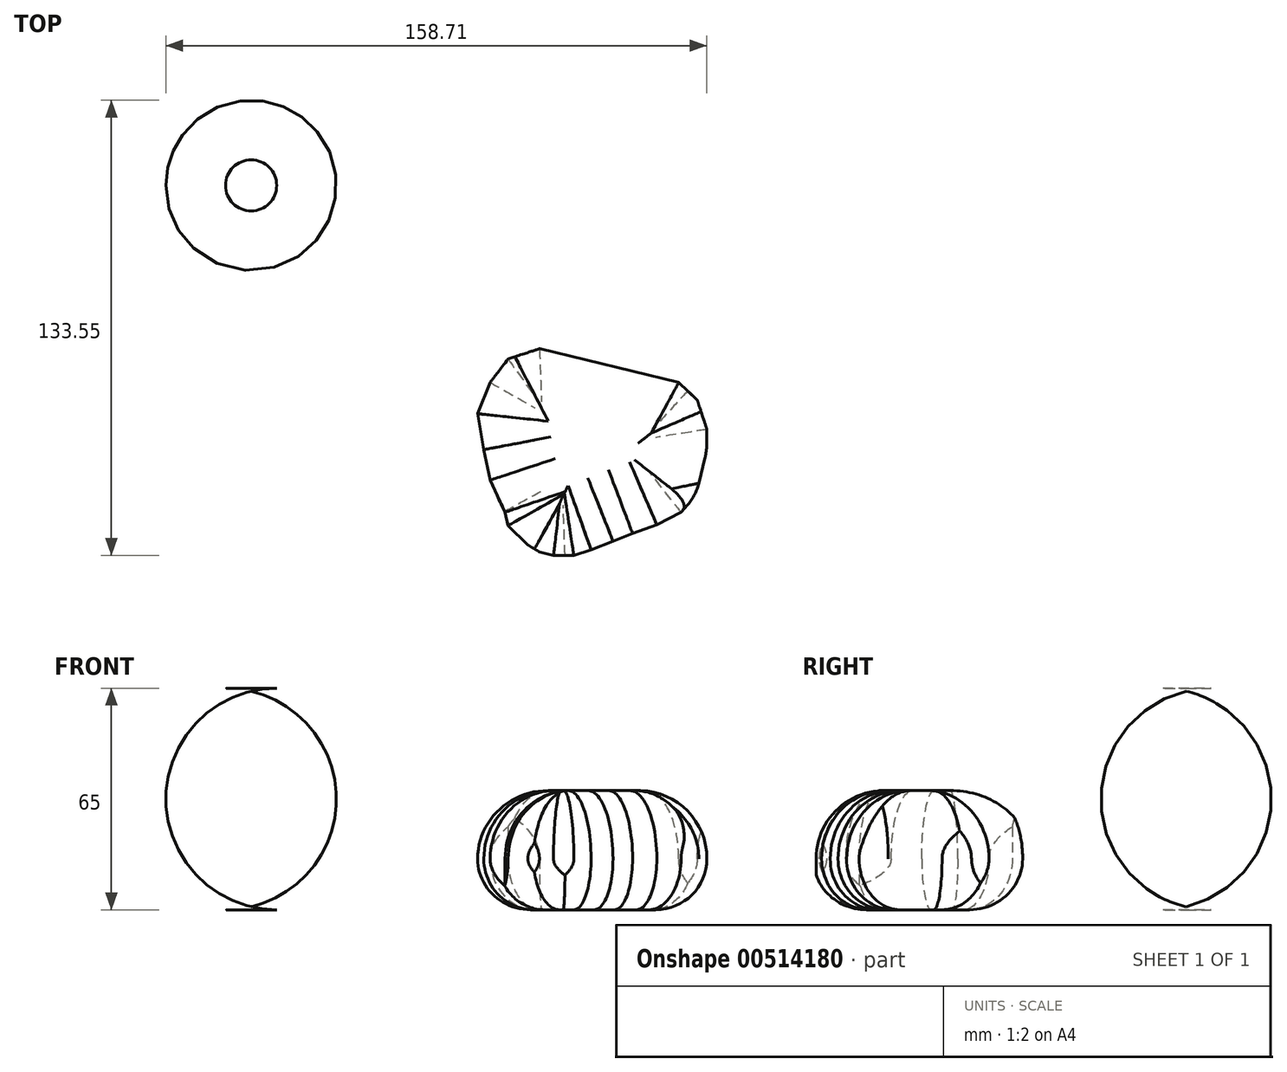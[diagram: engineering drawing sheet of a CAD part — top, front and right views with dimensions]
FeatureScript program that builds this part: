
annotation { "Feature Type Name" : "Feature", "Feature Type Description" : "" }
export const myFeature = defineFeature(function(context is Context, id is Id, definition is map)
    precondition{}
    {
        {
            var Q0;
            Q0=qCreatedBy(makeId("Top.planeOp"),FACE);
            var sketch = newSketch(context, id + "F0", { "sketchPlane" : qUnion([Q0])});
            skCircle(sketch, "E0", {"center": v(-39.49, 24.57) * mm, "radius": 45 * mm});
            skLineSegment(sketch, "E1", {"start": v(19.29, -34.44) * mm, "end": v(22.96, -25.26) * mm});
            skLineSegment(sketch, "E2", {"start": v(22.96, -25.26) * mm, "end": v(28.24, -18.37) * mm});
            skLineSegment(sketch, "E3", {"start": v(28.24, -18.37) * mm, "end": v(37.42, -15.38) * mm});
            skLineSegment(sketch, "E4", {"start": v(37.42, -15.38) * mm, "end": v(78.3, -25.26) * mm});
            skLineSegment(sketch, "E5", {"start": v(78.3, -25.26) * mm, "end": v(83.7, -30.4) * mm});
            skLineSegment(sketch, "E6", {"start": v(83.7, -30.4) * mm, "end": v(86.56, -39.03) * mm});
            skLineSegment(sketch, "E7", {"start": v(86.56, -39.03) * mm, "end": v(86.56, -45) * mm});
            skLineSegment(sketch, "E8", {"start": v(86.56, -45) * mm, "end": v(84.97, -51.55) * mm});
            skLineSegment(sketch, "E9", {"start": v(84.97, -51.55) * mm, "end": v(83.33, -58.36) * mm});
            skLineSegment(sketch, "E10", {"start": v(83.33, -58.36) * mm, "end": v(78.98, -63.37) * mm});
            skLineSegment(sketch, "E11", {"start": v(78.98, -63.37) * mm, "end": v(71.86, -67.04) * mm});
            skLineSegment(sketch, "E12", {"start": v(71.86, -67.04) * mm, "end": v(64.74, -69.57) * mm});
            skLineSegment(sketch, "E13", {"start": v(64.74, -69.57) * mm, "end": v(59, -71.86) * mm});
            skLineSegment(sketch, "E14", {"start": v(59, -71.86) * mm, "end": v(52.58, -74.39) * mm});
            skLineSegment(sketch, "E15", {"start": v(41.56, -76) * mm, "end": v(37.42, -75) * mm});
            skLineSegment(sketch, "E16", {"start": v(37.42, -75) * mm, "end": v(34.02, -72.92) * mm});
            skLineSegment(sketch, "E17", {"start": v(34.02, -72.92) * mm, "end": v(28.24, -67.27) * mm});
            skLineSegment(sketch, "E18", {"start": v(28.24, -67.27) * mm, "end": v(27.33, -63.37) * mm});
            skLineSegment(sketch, "E19", {"start": v(27.33, -63.37) * mm, "end": v(22.96, -53.96) * mm});
            skLineSegment(sketch, "E20", {"start": v(22.96, -53.96) * mm, "end": v(21.08, -45) * mm});
            skLineSegment(sketch, "E21", {"start": v(21.08, -45) * mm, "end": v(19.29, -34.44) * mm});
            skLineSegment(sketch, "E22", {"start": v(52.58, -74.39) * mm, "end": v(47.53, -76) * mm});
            skLineSegment(sketch, "E23", {"start": v(47.53, -76) * mm, "end": v(41.56, -76) * mm});
            skSolve(sketch);
        }
        {
            var Q0;
            Q0=makeQuery(id+"F0.imprint","IMPRINT",FACE,{"disambiguationData":[TD([[makeQuery(id+"F0.imprint","IMPRINT",EDGE,{"derivedFrom":sQuery(id+"F0.wireOp",EDGE,"E1")}),-1.0]])]});
            extrude(context, id + "F1", {"entities" : qUnion([Q0]), "depth" : 35 * mm});
        }
        {
            var Q0;
            Q0=makeQuery(id+"F1.opExtrude","CAP_EDGE",EDGE,{"disambiguationData":[OSD([sQuery(id+"F0.wireOp",EDGE,"E20")])],"isStart":false});
            var Q1;
            Q1=makeQuery(id+"F1.opExtrude","CAP_EDGE",EDGE,{"disambiguationData":[OSD([sQuery(id+"F0.wireOp",EDGE,"E1")])],"isStart":false});
            var Q2;
            Q2=makeQuery(id+"F1.opExtrude","CAP_EDGE",EDGE,{"disambiguationData":[OSD([sQuery(id+"F0.wireOp",EDGE,"E3")])],"isStart":false});
            var Q3;
            Q3=makeQuery(id+"F1.opExtrude","CAP_EDGE",EDGE,{"disambiguationData":[OSD([sQuery(id+"F0.wireOp",EDGE,"E4")])],"isStart":false});
            var Q4;
            Q4=makeQuery(id+"F1.opExtrude","CAP_EDGE",EDGE,{"disambiguationData":[OSD([sQuery(id+"F0.wireOp",EDGE,"E2")])],"isStart":false});
            var Q5;
            Q5=makeQuery(id+"F1.opExtrude","CAP_EDGE",EDGE,{"disambiguationData":[OSD([sQuery(id+"F0.wireOp",EDGE,"E5")])],"isStart":false});
            var Q6;
            Q6=makeQuery(id+"F1.opExtrude","SWEPT_EDGE",EDGE,{"disambiguationData":[OSD([sQuery(id+"F0.wireOp",EDGE,"E7"),sQuery(id+"F0.wireOp",EDGE,"E8")])]});
            var Q7;
            Q7=makeQuery(id+"F1.opExtrude","CAP_EDGE",EDGE,{"disambiguationData":[OSD([sQuery(id+"F0.wireOp",EDGE,"E7")])],"isStart":false});
            var Q8;
            Q8=makeQuery(id+"F1.opExtrude","CAP_EDGE",EDGE,{"disambiguationData":[OSD([sQuery(id+"F0.wireOp",EDGE,"E10")])],"isStart":false});
            var Q9;
            Q9=makeQuery(id+"F1.opExtrude","CAP_EDGE",EDGE,{"disambiguationData":[OSD([sQuery(id+"F0.wireOp",EDGE,"E8"),sQuery(id+"F0.wireOp",EDGE,"E9")])],"isStart":false});
            var Q10;
            Q10=makeQuery(id+"F1.opExtrude","CAP_EDGE",EDGE,{"disambiguationData":[OSD([sQuery(id+"F0.wireOp",EDGE,"E12")])],"isStart":false});
            var Q11;
            Q11=makeQuery(id+"F1.opExtrude","CAP_EDGE",EDGE,{"disambiguationData":[OSD([sQuery(id+"F0.wireOp",EDGE,"E11")])],"isStart":false});
            var Q12;
            Q12=makeQuery(id+"F1.opExtrude","CAP_EDGE",EDGE,{"disambiguationData":[OSD([sQuery(id+"F0.wireOp",EDGE,"E13")])],"isStart":false});
            var Q13;
            Q13=makeQuery(id+"F1.opExtrude","CAP_EDGE",EDGE,{"disambiguationData":[OSD([sQuery(id+"F0.wireOp",EDGE,"E23")])],"isStart":false});
            var Q14;
            Q14=makeQuery(id+"F1.opExtrude","CAP_EDGE",EDGE,{"disambiguationData":[OSD([sQuery(id+"F0.wireOp",EDGE,"E22")])],"isStart":false});
            var Q15;
            Q15=makeQuery(id+"F1.opExtrude","CAP_EDGE",EDGE,{"disambiguationData":[OSD([sQuery(id+"F0.wireOp",EDGE,"E14")])],"isStart":false});
            var Q16;
            Q16=makeQuery(id+"F1.opExtrude","CAP_EDGE",EDGE,{"disambiguationData":[OSD([sQuery(id+"F0.wireOp",EDGE,"E17")])],"isStart":false});
            var Q17;
            Q17=makeQuery(id+"F1.opExtrude","CAP_EDGE",EDGE,{"disambiguationData":[OSD([sQuery(id+"F0.wireOp",EDGE,"E18")])],"isStart":false});
            var Q18;
            Q18=makeQuery(id+"F1.opExtrude","CAP_EDGE",EDGE,{"disambiguationData":[OSD([sQuery(id+"F0.wireOp",EDGE,"E19")])],"isStart":false});
            var Q19;
            Q19=makeQuery(id+"F1.opExtrude","CAP_EDGE",EDGE,{"disambiguationData":[OSD([sQuery(id+"F0.wireOp",EDGE,"E15")])],"isStart":false});
            var Q20;
            Q20=makeQuery(id+"F1.opExtrude","CAP_EDGE",EDGE,{"disambiguationData":[OSD([sQuery(id+"F0.wireOp",EDGE,"E21")])],"isStart":false});
            fillet(context, id + "F2", {"entities" : qUnion([Q0, Q1, Q2, Q3, Q4, Q5, Q6, Q7, Q8, Q9, Q10, Q11, Q12, Q13, Q14, Q15, Q16, Q17, Q18, Q19, Q20]), "radius" : 20 * mm, "tangentPropagation" : true, "allowEdgeOverflow" : false});
        }
        {
            var Q0;
            Q0=makeQuery(id+"F1.opExtrude","SWEPT_FACE",FACE,{"disambiguationData":[OSD([sQuery(id+"F0.wireOp",EDGE,"E8"),sQuery(id+"F0.wireOp",EDGE,"E9")])]});
            var Q1;
            Q1=makeQuery(id+"F1.opExtrude","CAP_EDGE",EDGE,{"disambiguationData":[OSD([sQuery(id+"F0.wireOp",EDGE,"E11")])],"isStart":true});
            var Q2;
            Q2=makeQuery(id+"F1.opExtrude","CAP_EDGE",EDGE,{"disambiguationData":[OSD([sQuery(id+"F0.wireOp",EDGE,"E13")])],"isStart":true});
            var Q3;
            Q3=makeQuery(id+"F1.opExtrude","CAP_EDGE",EDGE,{"disambiguationData":[OSD([sQuery(id+"F0.wireOp",EDGE,"E16")])],"isStart":true});
            var Q4;
            Q4=makeQuery(id+"F1.opExtrude","CAP_EDGE",EDGE,{"disambiguationData":[OSD([sQuery(id+"F0.wireOp",EDGE,"E12")])],"isStart":true});
            var Q5;
            Q5=makeQuery(id+"F1.opExtrude","CAP_EDGE",EDGE,{"disambiguationData":[OSD([sQuery(id+"F0.wireOp",EDGE,"E10")])],"isStart":true});
            var Q6;
            Q6=makeQuery(id+"F1.opExtrude","CAP_EDGE",EDGE,{"disambiguationData":[OSD([sQuery(id+"F0.wireOp",EDGE,"E8"),sQuery(id+"F0.wireOp",EDGE,"E9")])],"isStart":true});
            var Q7;
            Q7=makeQuery(id+"F1.opExtrude","CAP_EDGE",EDGE,{"disambiguationData":[OSD([sQuery(id+"F0.wireOp",EDGE,"E15")])],"isStart":true});
            var Q8;
            Q8=makeQuery(id+"F1.opExtrude","CAP_EDGE",EDGE,{"disambiguationData":[OSD([sQuery(id+"F0.wireOp",EDGE,"E14")])],"isStart":true});
            var Q9;
            Q9=makeQuery(id+"F1.opExtrude","CAP_EDGE",EDGE,{"disambiguationData":[OSD([sQuery(id+"F0.wireOp",EDGE,"E20")])],"isStart":true});
            var Q10;
            Q10=makeQuery(id+"F1.opExtrude","CAP_EDGE",EDGE,{"disambiguationData":[OSD([sQuery(id+"F0.wireOp",EDGE,"E21")])],"isStart":true});
            var Q11;
            Q11=makeQuery(id+"F1.opExtrude","CAP_EDGE",EDGE,{"disambiguationData":[OSD([sQuery(id+"F0.wireOp",EDGE,"E1")])],"isStart":true});
            var Q12;
            Q12=makeQuery(id+"F1.opExtrude","CAP_EDGE",EDGE,{"disambiguationData":[OSD([sQuery(id+"F0.wireOp",EDGE,"E2")])],"isStart":true});
            var Q13;
            Q13=makeQuery(id+"F1.opExtrude","CAP_EDGE",EDGE,{"disambiguationData":[OSD([sQuery(id+"F0.wireOp",EDGE,"E4")])],"isStart":true});
            var Q14;
            Q14=makeQuery(id+"F1.opExtrude","CAP_EDGE",EDGE,{"disambiguationData":[OSD([sQuery(id+"F0.wireOp",EDGE,"E3")])],"isStart":true});
            var Q15;
            Q15=makeQuery(id+"F1.opExtrude","CAP_EDGE",EDGE,{"disambiguationData":[OSD([sQuery(id+"F0.wireOp",EDGE,"E5")])],"isStart":true});
            var Q16;
            Q16=makeQuery(id+"F1.opExtrude","CAP_EDGE",EDGE,{"disambiguationData":[OSD([sQuery(id+"F0.wireOp",EDGE,"E6")])],"isStart":true});
            var Q17;
            Q17=makeQuery(id+"F1.opExtrude","CAP_EDGE",EDGE,{"disambiguationData":[OSD([sQuery(id+"F0.wireOp",EDGE,"E17")])],"isStart":true});
            fillet(context, id + "F3", {"entities" : qUnion([Q0, Q1, Q2, Q3, Q4, Q5, Q6, Q7, Q8, Q9, Q10, Q11, Q12, Q13, Q14, Q15, Q16, Q17]), "radius" : 15 * mm, "tangentPropagation" : true, "allowEdgeOverflow" : false});
        }
        {
            var Q0;
            Q0=qCreatedBy(makeId("Top.planeOp"),FACE);
            var sketch = newSketch(context, id + "F4", { "sketchPlane" : qUnion([Q0])});
            skCircle(sketch, "E24", {"center": v(-47.15, 32.55) * mm, "radius": 40 * mm});
            skSolve(sketch);
        }
        {
            var Q0;
            Q0=makeQuery(id+"F4.imprint","IMPRINT",FACE,{"disambiguationData":[TD([[makeQuery(id+"F4.imprint","IMPRINT",EDGE,{"derivedFrom":sQuery(id+"F4.wireOp",EDGE,"E24")}),1.0]])]});
            extrude(context, id + "F5", {"entities" : qUnion([Q0]), "depth" : 40 * mm});
        }
        {
            var Q0;
            Q0=makeQuery(id+"F5.opExtrude","CAP_FACE",FACE,{"disambiguationData":[OSD([sQuery(id+"F4.wireOp",EDGE,"E24")])],"isStart":false});
            extrude(context, id + "F6", {"entities" : qUnion([Q0]), "operationType" : NewBodyOperationType.ADD, "depth" : 25 * mm});
        }
        {
            var Q0;
            {var subQ0=sQuery(id+"F4.wireOp",EDGE,"E24");Q0=makeQuery(id+"F6.boolean.opBoolean","MERGE",FACE,{"derivedFrom":[makeQuery(id+"F5.opExtrude","SWEPT_FACE",FACE,{"disambiguationData":[OSD([subQ0])]}),makeQuery(id+"F6.opExtrude","SWEPT_FACE",FACE,{"disambiguationData":[OSD([subQ0])]})]});}
            var Q1;
            Q1=makeQuery(id+"F6.opExtrude","CAP_EDGE",EDGE,{"disambiguationData":[OSD([sQuery(id+"F4.wireOp",EDGE,"E24")])],"isStart":false});
            fillet(context, id + "F7", {"entities" : qUnion([Q0, Q1]), "radius" : 32.5 * mm, "tangentPropagation" : true, "allowEdgeOverflow" : false});
        }
    });
